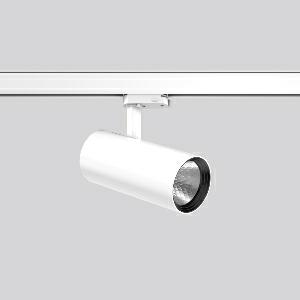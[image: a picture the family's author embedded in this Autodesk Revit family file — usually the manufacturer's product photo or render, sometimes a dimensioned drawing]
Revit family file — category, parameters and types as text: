
# Revit family: deecos_s_mini_742204_002_2_76_b97b
name_source: partatom
category: Lighting Fixtures
units: mm (PartAtom-declared; Revit-internal decimal feet)

## family parameters
Cut with Voids When Loaded = No
Host = Face
Light Source = No
Part Type = Normal
Room Calculation Point = No
Round Connector Dimension = Use Diameter
Shared = No

## types (1)
- DEECOS S mini (1 x LED Modul 927, 3300 lm, 2700)
    Apparent Load = 29 VA
    Approval mark = CE
    CIE Flux Codes = 99 100 100 100 100
    Color Rendering = 92
    Color Temperature = 2700
    Default Elevation = 1800 mm
    Description = Series: DEECOS S mini
LED surface-mounted projector in modern design with no visible cooling ribs. Housing: die-cast aluminium, powder-coated. Rotation range: 356°. Swivel range: 90°. Black plastic ring and recessed LED to prevent glare from the side. Optical assembly with reflector made of MIRO-Silver with 98% total light reflection for outstanding efficiency - can be changed without tools. Best colour rendering index Ra>90. With adapter for RZB 3-circuit DALI tracks. Suitable for Track on ceiling, Wall track. High quality converter without flickering and stroboscopic effect. The following accessories can be mounted without use of tools: interchangeable lenses, decorative glasses, honeycomb louvre, clear and frosted diffusers, white interchangeable plastic ring. 
Colour: traffic white, matt (RAL 9016)
Diameter: 87 mm
Height: 214 mm
Lamp: LED
Socket: without socket
Colour temperature: 2700K
Colour rendering index (CRI): 92
System power: 29 W
Rated luminous flux: 3300 lm
Luminous efficiency: 114 lm/W
Control gear: Converter, dimmable, DALI
Protection class: I
Type of protection: IP 20
    Height = 214 mm
    Lamp = 1 x LED Modul 927
    Lamp Light Flux = 3300 lm
    Lamp count = 1
    Length = 87 mm
    Lifetime = 50000 h
    Luminous efficacy = 114 lm/W
    Manufacturer = RZB
    ModVariant = No
    Model = 742204.002.2.76
    Mounting Place = Ceiling
    Mounting Type = Rail mounted
    Number of Poles = 1
    OnlyDefault = Yes
    Power Factor = 1
    Product Name = DEECOS S mini
    Product group = Track mounted projectors
    ProductGroupID = 301
    Protection Class = Protection class I
    Protection Degree = IP 20
    RLX_Detail_Level = 1
    RLX_Emergency_Light_Flux = 0 lm
    RLX_Emergency_Type = 0
    RLX_Emergency_Type_DB = No
    RlxData = <blob elided: 35225 chars, md5=6bea6ca1>
    Socket = socket
    Standby Power = 0 W
    System Light Flux = 3300 lm
    System Power = 29 W
    Type Comments = Product without accessories
    Type Image = 741926.002.jpg
    URL = http://relux.com
    VarID = ---
    Voltage = 230 V
    Voltage Range = 220-240 V
    Weight = 0.00 kg
    Width = 0 mm  [stored 0 ft]

note: [stored X ft] marks values corroborated as IEEE doubles in the binary element streams (Revit-internal decimal feet)

## geometry (parser evidence)
native form markers: Blend x4, Sweep x13
no freeform markers — native parametric forms only
